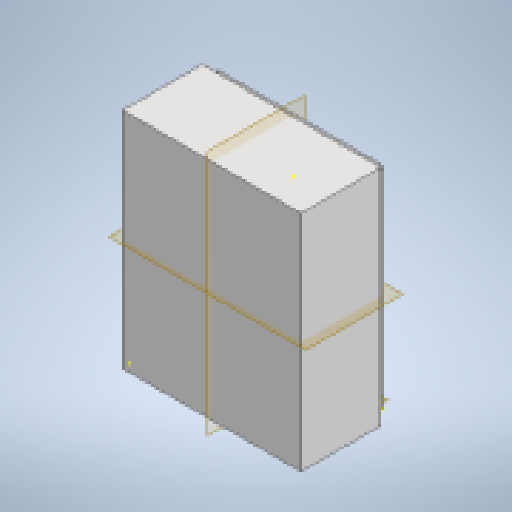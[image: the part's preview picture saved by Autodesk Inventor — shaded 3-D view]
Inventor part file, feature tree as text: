
AUTODESK INVENTOR PART (.ipt)
format: ipt  version: 2023 (Build 270158030, 158C)  size: 360,960 bytes
history: native  units: mm
features: sketch x9, other x8, extrude x7, projected_geometry x6, loft x4, plane x3, mirror x2, fillet x2, pattern_linear x1
ambient origin geometry x8: Origin, YZ Plane, XZ Plane, XY Plane, X Axis, Y Axis, Z Axis, Center Point
bodies: Solid1 (feature_tree)
feature tree (42):
  extrude  "Extrusion1"  Depth=495.0mm
  extrude  "Extrusion2"  Depth=1.6mm
  extrude  "Extrusion3"  Depth=18.9mm
  extrude  "Extrusion4"  Depth=1.6mm
  extrude  "Extrusion5"  Depth=6.0mm
  extrude  "Extrusion6"  Depth=13.0mm TaperAngle=0.0deg
  plane  "Work Plane3"
  plane  "Work Plane4"
  mirror  "Mirror1"
  mirror  "Mirror2"
  sketch  "Sketch8"  dims[d21=45.0deg d22=6.0mm]
  sketch  "Sketch9"  dims[d23=10.0mm d24=0.0mm d25=0.0mm d26=90.0deg]
  loft  "Loft1"
  loft  "Loft2"
  loft  "Loft3"
  loft  "Loft4"
  fillet  "Fillet2"  [1 undecoded]
  plane  "Work Plane5"
  extrude  "Extrusion7"  TaperAngle=0.0deg  [1 undecoded]
  pattern_linear  "Rectangular Pattern1"  Spacing1=0.0mm  [1 undecoded]
  fillet  "Fillet1"  [1 undecoded]
  sketch  "Sketch1"  dims[d0=395.0mm d1=495.0mm]
  sketch  "Sketch2"  dims[d6=1.6mm d7=0.0mm d8=1.6mm]
  projected_geometry  "Projected Loop1"
  sketch  "Sketch3"  dims[d9=173.0mm d10=0.0mm d11=18.9mm]
  projected_geometry  "Projected Loop2"
  sketch  "Sketch4"  dims[d12=1.6mm d13=0.0mm d14=1.6mm]
  projected_geometry  "Projected Loop3"
  sketch  "Sketch6"  dims[d15=13.0mm d16=0.0mm d17=6.0mm]
  sketch  "Sketch7"  dims[d18=45.0deg d19=13.0mm d20=0.0mm]
  projected_geometry  "Projected Loop4"
  projected_geometry  "Projected Loop5"
  projected_geometry  "Projected Loop6"
  other  "Edges1"
  other  "Edges2"
  other  "Edges3"
  other  "Edges4"
  other  "Edges5"
  other  "Edges6"
  other  "Edges7"
  other  "Edges8"
  sketch  "Sketch10"  dims[d27=0.0mm d28=90.0deg d29=8.0mm d30=0.0mm d31=90.0deg d32=0.0mm d33=90.0deg d34=0.0mm d35=90.0deg d36=0.0mm d37=90.0deg d38=0.0mm d39=90.0deg d40=0.0mm d41=90.0deg d42=8.0mm d43=-25.0mm d44=0.8mm d45=0.8mm d46=1.0mm d47=0.8mm d48=0.8mm d49=4.3mm d50=22.68928mm d51=13.0mm d52=7.0mm d53=2.069249mm d54=10.0mm d55=0.0mm d56=20.0mm d58=390.0mm d2=0.5mm d3=0.872665mm]
note: 4 required parameter values undecoded (feature->parameter linkage not recoverable at this tier; creation-order binding heuristic only, values carry confidence <= 0.55)
